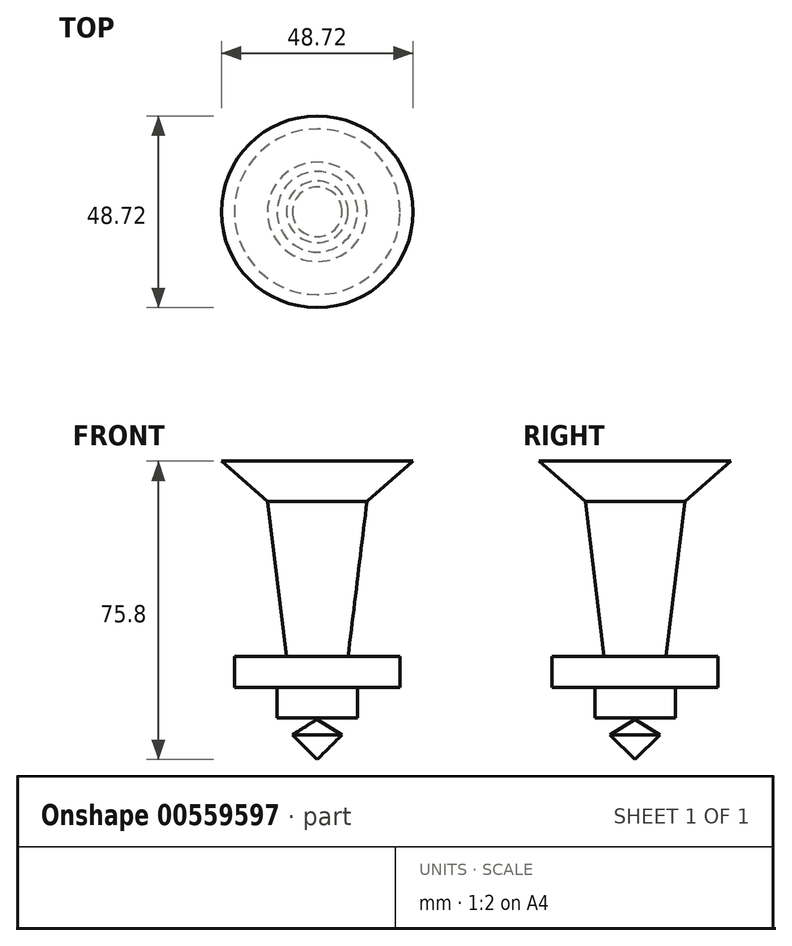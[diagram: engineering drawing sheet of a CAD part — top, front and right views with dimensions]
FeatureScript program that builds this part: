
annotation { "Feature Type Name" : "Feature", "Feature Type Description" : "" }
export const myFeature = defineFeature(function(context is Context, id is Id, definition is map)
    precondition{}
    {
        {
            var Q0;
            Q0=qCreatedBy(makeId("Front.planeOp"),FACE);
            var sketch = newSketch(context, id + "F0", { "sketchPlane" : qUnion([Q0])});
            skLineSegment(sketch, "E0", {"start": v(0, 0) * mm, "end": v(0, -65.27) * mm});
            skLineSegment(sketch, "E1", {"start": v(0, -65.27) * mm, "end": v(-10.23, -65.27) * mm});
            skLineSegment(sketch, "E2", {"start": v(-10.23, -65.27) * mm, "end": v(-10.23, -57.45) * mm});
            skLineSegment(sketch, "E3", {"start": v(-10.23, -57.45) * mm, "end": v(-21.06, -57.45) * mm});
            skLineSegment(sketch, "E4", {"start": v(-21.06, -57.45) * mm, "end": v(-21.06, -49.63) * mm});
            skLineSegment(sketch, "E5", {"start": v(-21.06, -49.63) * mm, "end": v(-7.82, -49.63) * mm});
            skLineSegment(sketch, "E6", {"start": v(-7.82, -49.63) * mm, "end": v(-12.63, -10.23) * mm});
            skLineSegment(sketch, "E7", {"start": v(-12.63, -10.23) * mm, "end": v(-24.36, 0) * mm});
            skLineSegment(sketch, "E8", {"start": v(-24.36, 0) * mm, "end": v(0, 0) * mm});
            skSolve(sketch);
        }
        {
            var Q0;
            Q0=makeQuery(id+"F0.imprint","IMPRINT",FACE,{"disambiguationData":[TD([[makeQuery(id+"F0.imprint","IMPRINT",EDGE,{"derivedFrom":sQuery(id+"F0.wireOp",EDGE,"E0")}),-1.0]])]});
            var Q1;
            Q1=sQuery(id+"F0.wireOp",EDGE,"E0");
            revolve(context, id + "F1", {"entities" : qUnion([Q0]), "axis" : qUnion([Q1]), "revolveType" : RevolveType.FULL});
        }
        {
            var Q0;
            Q0=qCreatedBy(makeId("Front.planeOp"),FACE);
            var sketch = newSketch(context, id + "F2", { "sketchPlane" : qUnion([Q0])});
            skLineSegment(sketch, "E9", {"start": v(0, -65.57) * mm, "end": v(0, -65.57) * mm});
            skLineSegment(sketch, "E10", {"start": v(0, -65.57) * mm, "end": v(6.32, -69.48) * mm});
            skLineSegment(sketch, "E11", {"start": v(6.32, -69.48) * mm, "end": v(0, -75.8) * mm});
            skLineSegment(sketch, "E12", {"start": v(0, -75.8) * mm, "end": v(0, -65.57) * mm});
            skSolve(sketch);
        }
        {
            var Q0;
            Q0=makeQuery(id+"F2.imprint","IMPRINT",FACE,{"disambiguationData":[TD([[makeQuery(id+"F2.imprint","IMPRINT",EDGE,{"derivedFrom":sQuery(id+"F2.wireOp",EDGE,"E10")}),-1.0]])]});
            var Q1;
            Q1=sQuery(id+"F2.wireOp",EDGE,"E12");
            revolve(context, id + "F3", {"entities" : qUnion([Q0]), "axis" : qUnion([Q1]), "revolveType" : RevolveType.FULL});
        }
    });
